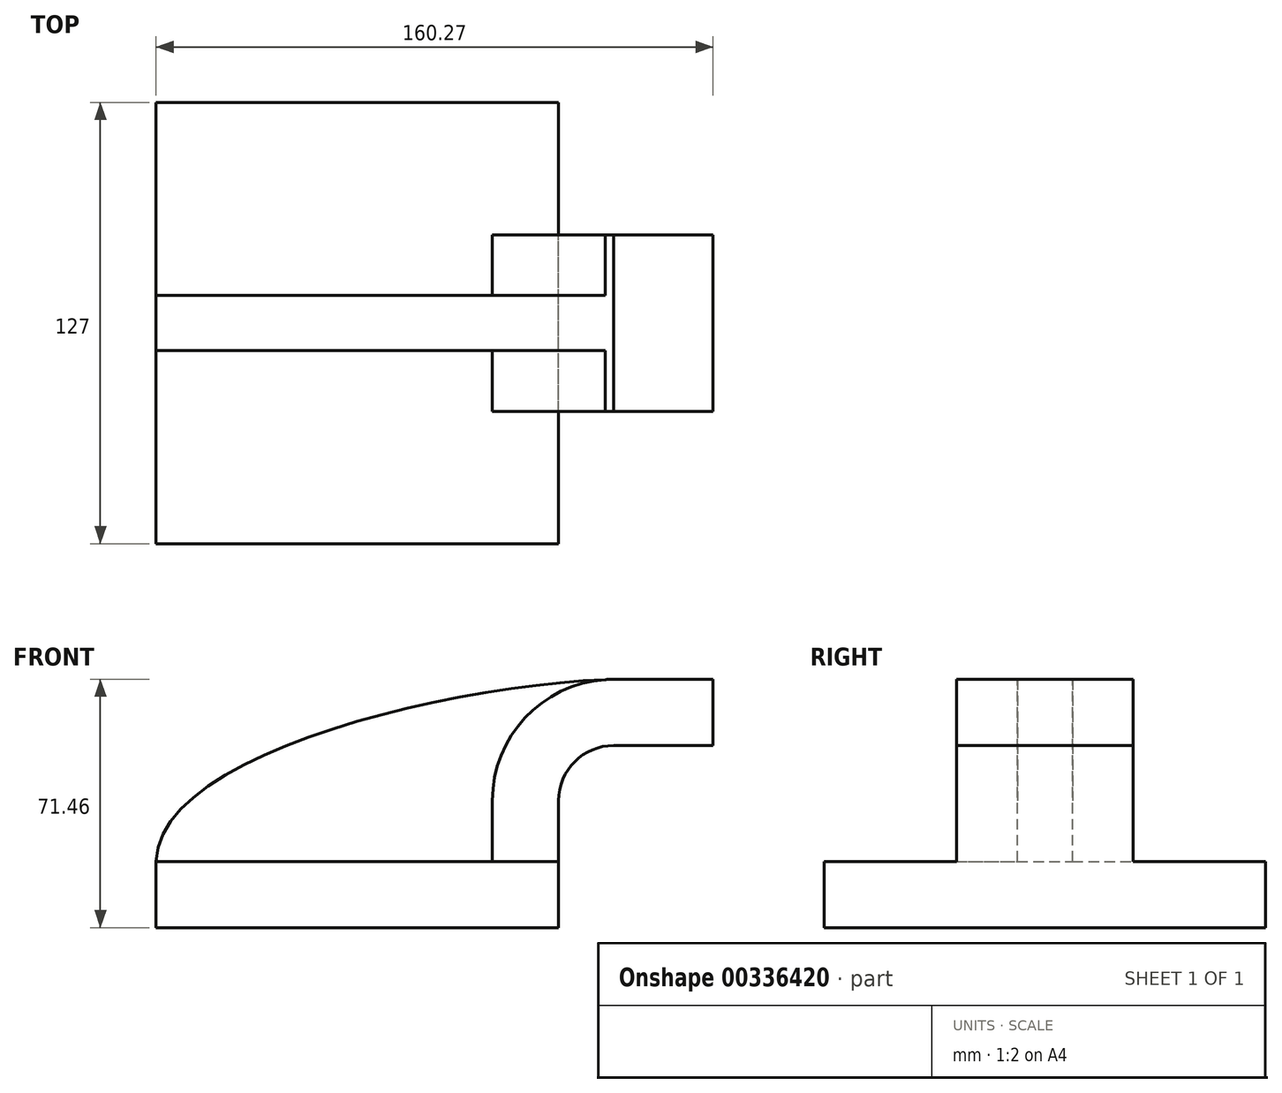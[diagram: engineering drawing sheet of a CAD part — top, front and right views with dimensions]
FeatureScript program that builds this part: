
annotation { "Feature Type Name" : "Feature", "Feature Type Description" : "" }
export const myFeature = defineFeature(function(context is Context, id is Id, definition is map)
    precondition{}
    {
        {
            var Q0;
            Q0=qCreatedBy(makeId("Front.planeOp"),FACE);
            var sketch = newSketch(context, id + "F0", { "sketchPlane" : qUnion([Q0])});
            skLineSegment(sketch, "E0.bottom", {"start": v(-57.91, 9.53) * mm, "end": v(57.91, 9.53) * mm});
            skLineSegment(sketch, "E0.top", {"start": v(-57.91, -9.52) * mm, "end": v(57.91, -9.52) * mm});
            skLineSegment(sketch, "E0.left", {"start": v(-57.91, 9.52) * mm, "end": v(-57.91, -9.53) * mm});
            skLineSegment(sketch, "E0.right", {"start": v(57.91, 9.53) * mm, "end": v(57.91, -9.52) * mm});
            skPoint(sketch, "E0.middle", {"position": v(0, 0) * mm});
            skLineSegment(sketch, "E1.bottom", {"start": v(76.96, 66.68) * mm, "end": v(127.76, 66.68) * mm});
            skLineSegment(sketch, "E1.top", {"start": v(76.96, 38.1) * mm, "end": v(127.76, 38.1) * mm});
            skLineSegment(sketch, "E1.left", {"start": v(76.96, 66.68) * mm, "end": v(76.96, 38.1) * mm});
            skLineSegment(sketch, "E1.right", {"start": v(127.76, 66.68) * mm, "end": v(127.76, 38.1) * mm});
            skPoint(sketch, "E1.middle", {"position": v(102.36, 52.39) * mm});
            skLineSegment(sketch, "E2", {"start": v(57.91, 9.53) * mm, "end": v(57.91, 27) * mm});
            skArc(sketch, "E3", {"start": v(57.91, 27) * mm, "mid": v(62.56, 38.23) * mm, "end": v(73.79, 42.88) * mm});
            skLineSegment(sketch, "E4", {"start": v(73.79, 42.88) * mm, "end": v(102.36, 42.88) * mm});
            skLineSegment(sketch, "E5.0", {"start": v(73.79, 61.93) * mm, "end": v(102.36, 61.93) * mm});
            skArc(sketch, "E5.1", {"start": v(38.86, 27) * mm, "mid": v(49.1, 51.7) * mm, "end": v(73.79, 61.93) * mm});
            skLineSegment(sketch, "E5.2", {"start": v(38.86, 9.53) * mm, "end": v(38.86, 27) * mm});
            skLineSegment(sketch, "E6", {"start": v(102.36, 42.88) * mm, "end": v(102.36, 66.68) * mm});
            skFitSpline(sketch, "E7", {"points": [v(-57.91, 9.53) * mm, v(73.79, 61.93) * mm], "startDerivative": vector(2.18, 93.89) * mm, "endDerivative": vector(139.7, 4.05) * mm});
            skSolve(sketch);
        }
        {
            var Q0;
            Q0=makeQuery(id+"F0.imprint","IMPRINT",FACE,{"disambiguationData":[TD([[makeQuery(id+"F0.imprint","IMPRINT",EDGE,{"derivedFrom":sQuery(id+"F0.wireOp",EDGE,"E0.top")}),1.0]])]});
            extrude(context, id + "F1", {"entities" : qUnion([Q0]), "endBound" : BoundingType.SYMMETRIC, "depth" : 127 * mm});
        }
        {
            var Q0;
            {var subQ6=sQuery(id+"F0.wireOp",EDGE,"E2");Q0=makeQuery(id+"F0.imprint","IMPRINT",FACE,{"disambiguationData":[TD([[makeQuery(id+"F0.imprint","IMPRINT",EDGE,{"derivedFrom":subQ6}),1.0]])]});}
            var Q1;
            {var subQ0=sQuery(id+"F0.wireOp",EDGE,"E5.0");var subQ1=sQuery(id+"F0.wireOp",EDGE,"E1.left");var subQ2=makeQuery(id+"F0.imprint","INTERSECT",VERTEX,{"derivedFrom":[subQ1,subQ0]});Q1=makeQuery(id+"F0.imprint","IMPRINT",FACE,{"disambiguationData":[TD([[makeQuery(id+"F0.imprint","IMPRINT",EDGE,{"disambiguationData":[TD([[subQ2,-1.0]])],"derivedFrom":subQ1}),1.0]])]});}
            extrude(context, id + "F2", {"entities" : qUnion([Q0, Q1]), "operationType" : NewBodyOperationType.ADD, "endBound" : BoundingType.SYMMETRIC, "depth" : 50.8 * mm});
        }
        {
            var Q0;
            {var subQ3=sQuery(id+"F0.wireOp",EDGE,"E5.2");Q0=makeQuery(id+"F0.imprint","IMPRINT",FACE,{"disambiguationData":[TD([[makeQuery(id+"F0.imprint","IMPRINT",EDGE,{"derivedFrom":subQ3}),1.0]])]});}
            extrude(context, id + "F3", {"entities" : qUnion([Q0]), "operationType" : NewBodyOperationType.ADD, "endBound" : BoundingType.SYMMETRIC, "depth" : 15.88 * mm});
        }
        {
            var Q0;
            Q0=sQuery(id+"F0.wireOp",EDGE,"E1.left");
            var Q1;
            Q1=sQuery(id+"F0.wireOp",EDGE,"E1.right");
            var Q2;
            Q2=sQuery(id+"F0.wireOp",EDGE,"E6");
            revolve(context, id + "F4", {"bodyType" : ToolBodyType.SURFACE, "surfaceEntities" : qUnion([Q0, Q1]), "axis" : qUnion([Q2]), "revolveType" : RevolveType.FULL});
        }
    });
